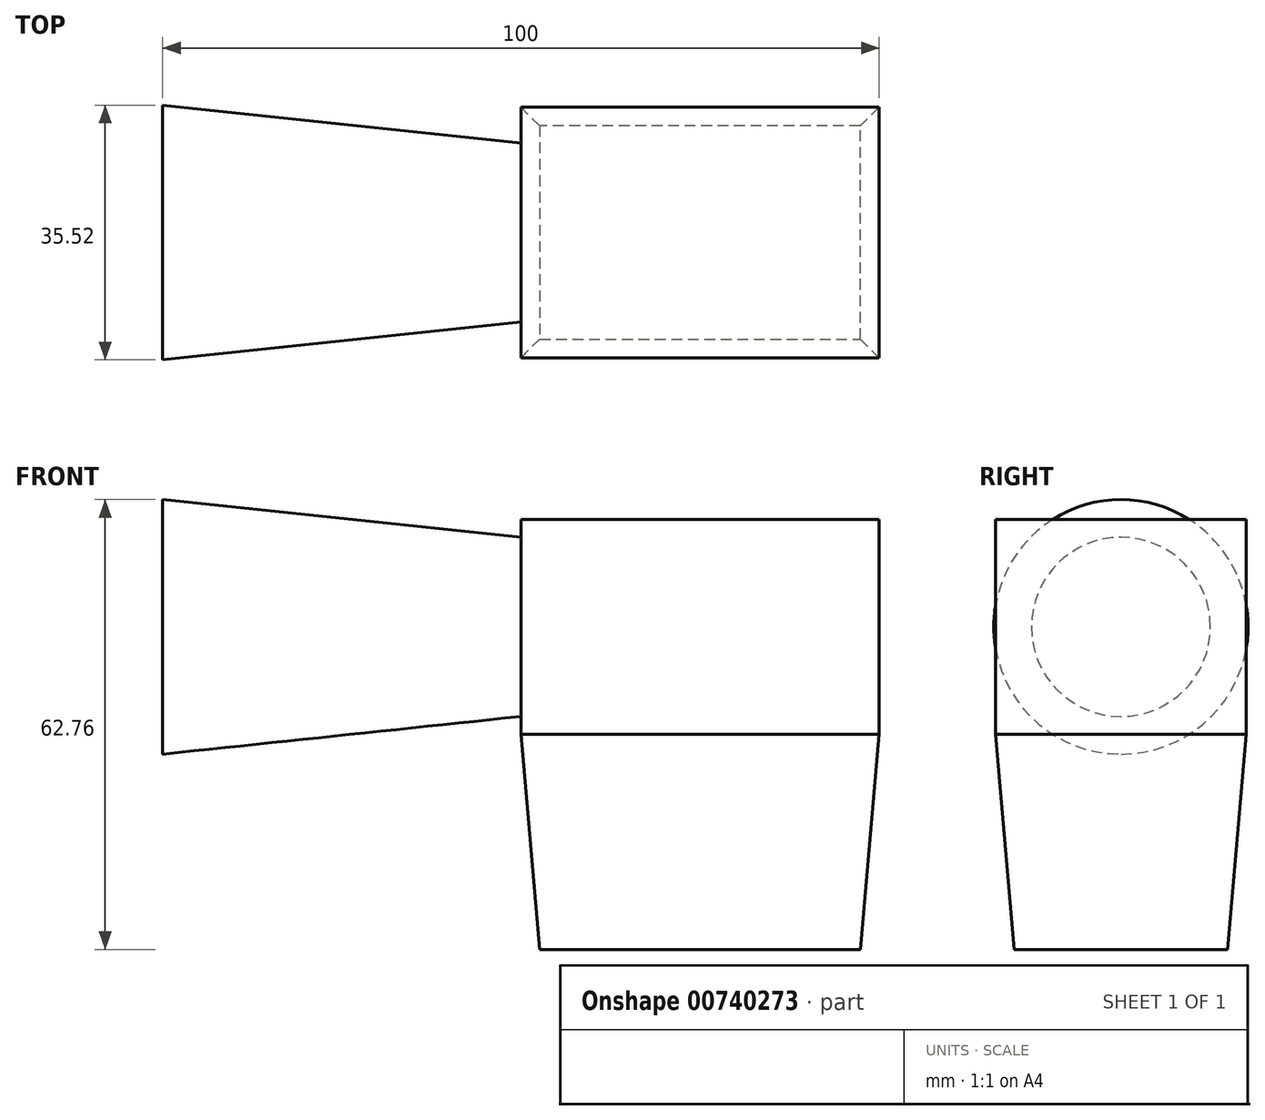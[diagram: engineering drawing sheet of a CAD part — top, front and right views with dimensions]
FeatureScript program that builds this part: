
annotation { "Feature Type Name" : "Feature", "Feature Type Description" : "" }
export const myFeature = defineFeature(function(context is Context, id is Id, definition is map)
    precondition{}
    {
        {
            var Q0;
            Q0=qCreatedBy(makeId("Front.planeOp"),FACE);
            var sketch = newSketch(context, id + "F0", { "sketchPlane" : qUnion([Q0])});
            skLineSegment(sketch, "E0.bottom", {"start": v(0, 0) * mm, "end": v(50, 0) * mm});
            skLineSegment(sketch, "E0.top", {"start": v(0, 30) * mm, "end": v(50, 30) * mm});
            skLineSegment(sketch, "E0.left", {"start": v(0, 0) * mm, "end": v(0, 30) * mm});
            skLineSegment(sketch, "E0.right", {"start": v(50, 0) * mm, "end": v(50, 30) * mm});
            skSolve(sketch);
        }
        {
            var Q0;
            Q0 = qSketchRegion(id + "F0", true);
            extrude(context, id + "F1", {"entities" : qUnion([Q0]), "endBound" : BoundingType.SYMMETRIC, "depth" : 35 * mm, "offsetDistance" : 25 * mm});
        }
        {
            var Q0;
            Q0=makeQuery(id+"F1.opExtrude","SWEPT_FACE",FACE,{"disambiguationData":[OSD([sQuery(id+"F0.wireOp",EDGE,"E0.bottom")])]});
            extrude(context, id + "F2", {"entities" : qUnion([Q0]), "depth" : 30 * mm, "offsetDistance" : 25 * mm, "hasDraft" : true, "draftAngle" : 5 * degree, "draftPullDirection" : true});
        }
        {
            var Q0;
            Q0=qCreatedBy(makeId("Right.planeOp"),FACE);
            var sketch = newSketch(context, id + "F3", { "sketchPlane" : qUnion([Q0])});
            skCircle(sketch, "E1", {"center": v(0, 15) * mm, "radius": 12.5 * mm});
            skSolve(sketch);
        }
        {
            var Q0;
            Q0=makeQuery(id+"F3.imprint","IMPRINT",FACE,{"disambiguationData":[TD([[makeQuery(id+"F3.imprint","IMPRINT",EDGE,{"derivedFrom":sQuery(id+"F3.wireOp",EDGE,"E1")}),1.0]])]});
            extrude(context, id + "F4", {"entities" : qUnion([Q0]), "oppositeDirection" : true, "depth" : 50 * mm, "offsetDistance" : 25 * mm, "hasDraft" : true, "draftAngle" : 6 * degree});
        }
    });
